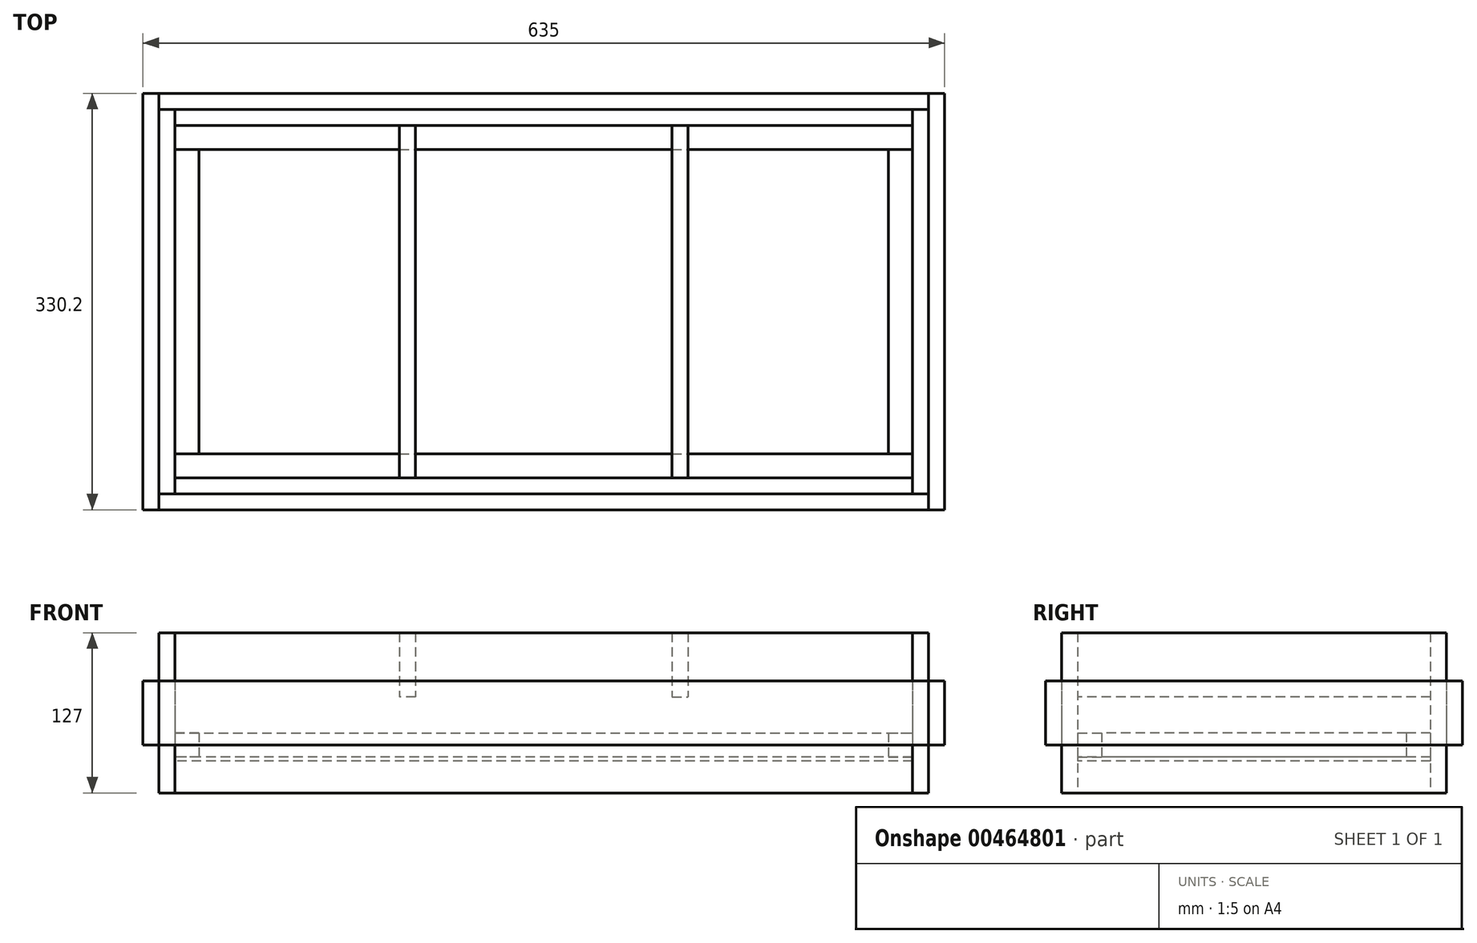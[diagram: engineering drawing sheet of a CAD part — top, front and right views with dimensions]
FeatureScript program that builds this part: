
annotation { "Feature Type Name" : "Feature", "Feature Type Description" : "" }
export const myFeature = defineFeature(function(context is Context, id is Id, definition is map)
    precondition{}
    {
        {
            var Q0;
            Q0=qCreatedBy(makeId("Top.planeOp"),FACE);
            var sketch = newSketch(context, id + "F0", { "sketchPlane" : qUnion([Q0])});
            skLineSegment(sketch, "E0.bottom", {"start": v(292.1, 139.7) * mm, "end": v(-292.1, 139.7) * mm});
            skLineSegment(sketch, "E0.top", {"start": v(292.1, -139.7) * mm, "end": v(-292.1, -139.7) * mm});
            skLineSegment(sketch, "E0.left", {"start": v(292.1, 139.7) * mm, "end": v(292.1, -139.7) * mm});
            skLineSegment(sketch, "E0.right", {"start": v(-292.1, 139.7) * mm, "end": v(-292.1, -139.7) * mm});
            skPoint(sketch, "E0.middle", {"position": v(0, 0) * mm});
            skLineSegment(sketch, "E1", {"start": v(-292.1, 0) * mm, "end": v(292.1, 0) * mm, "construction": true});
            skLineSegment(sketch, "E2", {"start": v(0, 139.7) * mm, "end": v(0, -139.7) * mm, "construction": true});
            skSolve(sketch);
        }
        {
            var Q0;
            Q0 = qSketchRegion(id + "F0", true);
            extrude(context, id + "F1", {"entities" : qUnion([Q0]), "depth" : 3.17 * mm});
        }
        {
            var Q0;
            Q0=qCreatedBy(makeId("Top.planeOp"),FACE);
            var sketch = newSketch(context, id + "F2", { "sketchPlane" : qUnion([Q0])});
            skLineSegment(sketch, "E3.bottom", {"start": v(-292.1, 139.7) * mm, "end": v(292.1, 139.7) * mm});
            skLineSegment(sketch, "E3.top", {"start": v(-292.1, 152.4) * mm, "end": v(292.1, 152.4) * mm});
            skLineSegment(sketch, "E3.left", {"start": v(-292.1, 139.7) * mm, "end": v(-292.1, 152.4) * mm});
            skLineSegment(sketch, "E3.right", {"start": v(292.1, 139.7) * mm, "end": v(292.1, 152.4) * mm});
            skSolve(sketch);
        }
        {
            var Q0;
            Q0 = qSketchRegion(id + "F2", true);
            extrude(context, id + "F3", {"entities" : qUnion([Q0]), "depth" : 101.6 * mm, "hasSecondDirection" : true, "secondDirectionOppositeDirection" : true, "secondDirectionDepth" : 25.4 * mm});
        }
        {
            var Q0;
            Q0=makeQuery(id+"F3.opExtrude","SWEPT_BODY",BODY,{"disambiguationData":[OSD([sQuery(id+"F2.wireOp",EDGE,"E3.bottom"),sQuery(id+"F2.wireOp",EDGE,"E3.top"),sQuery(id+"F2.wireOp",EDGE,"E3.left"),sQuery(id+"F2.wireOp",EDGE,"E3.right")])]});
            var Q1;
            Q1=qCreatedBy(makeId("Front.planeOp"),FACE);
            mirror(context, id + "F4", {"entities" : qUnion([Q0]), "mirrorPlane" : qUnion([Q1])});
        }
        {
            var Q0;
            Q0=qCreatedBy(makeId("Top.planeOp"),FACE);
            var sketch = newSketch(context, id + "F5", { "sketchPlane" : qUnion([Q0])});
            skLineSegment(sketch, "E4.bottom", {"start": v(292.1, 152.4) * mm, "end": v(304.8, 152.4) * mm});
            skLineSegment(sketch, "E4.top", {"start": v(292.1, -152.4) * mm, "end": v(304.8, -152.4) * mm});
            skLineSegment(sketch, "E4.left", {"start": v(292.1, 152.4) * mm, "end": v(292.1, -152.4) * mm});
            skLineSegment(sketch, "E4.right", {"start": v(304.8, 152.4) * mm, "end": v(304.8, -152.4) * mm});
            skSolve(sketch);
        }
        {
            var Q0;
            Q0 = qSketchRegion(id + "F5", true);
            extrude(context, id + "F6", {"entities" : qUnion([Q0]), "depth" : 101.6 * mm, "hasSecondDirection" : true, "secondDirectionOppositeDirection" : true, "secondDirectionDepth" : 25.4 * mm});
        }
        {
            var Q0;
            Q0=makeQuery(id+"F6.opExtrude","SWEPT_BODY",BODY,{"disambiguationData":[OSD([sQuery(id+"F5.wireOp",EDGE,"E4.bottom"),sQuery(id+"F5.wireOp",EDGE,"E4.top"),sQuery(id+"F5.wireOp",EDGE,"E4.left"),sQuery(id+"F5.wireOp",EDGE,"E4.right")])]});
            var Q1;
            Q1=qCreatedBy(makeId("Right.planeOp"),FACE);
            mirror(context, id + "F7", {"entities" : qUnion([Q0]), "mirrorPlane" : qUnion([Q1])});
        }
        {
            var Q0;
            Q0=qCreatedBy(makeId("Top.planeOp"),FACE);
            var sketch = newSketch(context, id + "F8", { "sketchPlane" : qUnion([Q0])});
            skLineSegment(sketch, "E5.bottom", {"start": v(-304.8, 165.1) * mm, "end": v(304.8, 165.1) * mm});
            skLineSegment(sketch, "E5.top", {"start": v(-304.8, 152.4) * mm, "end": v(304.8, 152.4) * mm});
            skLineSegment(sketch, "E5.left", {"start": v(-304.8, 165.1) * mm, "end": v(-304.8, 152.4) * mm});
            skLineSegment(sketch, "E5.right", {"start": v(304.8, 165.1) * mm, "end": v(304.8, 152.4) * mm});
            skSolve(sketch);
        }
        {
            var Q0;
            Q0 = qSketchRegion(id + "F8", true);
            extrude(context, id + "F9", {"entities" : qUnion([Q0]), "depth" : 63.5 * mm, "hasSecondDirection" : true, "secondDirectionOppositeDirection" : false, "secondDirectionDepth" : 12.7 * mm});
        }
        {
            var Q0;
            Q0=makeQuery(id+"F9.opExtrude","SWEPT_BODY",BODY,{"disambiguationData":[OSD([sQuery(id+"F8.wireOp",EDGE,"E5.bottom"),sQuery(id+"F8.wireOp",EDGE,"E5.top"),sQuery(id+"F8.wireOp",EDGE,"E5.left"),sQuery(id+"F8.wireOp",EDGE,"E5.right")])]});
            var Q1;
            Q1=qCreatedBy(makeId("Front.planeOp"),FACE);
            mirror(context, id + "F10", {"entities" : qUnion([Q0]), "mirrorPlane" : qUnion([Q1])});
        }
        {
            var Q0;
            Q0=qCreatedBy(makeId("Top.planeOp"),FACE);
            var sketch = newSketch(context, id + "F11", { "sketchPlane" : qUnion([Q0])});
            skLineSegment(sketch, "E6.bottom", {"start": v(304.8, 165.1) * mm, "end": v(317.5, 165.1) * mm});
            skLineSegment(sketch, "E6.top", {"start": v(304.8, -165.1) * mm, "end": v(317.5, -165.1) * mm});
            skLineSegment(sketch, "E6.left", {"start": v(304.8, 165.1) * mm, "end": v(304.8, -165.1) * mm});
            skLineSegment(sketch, "E6.right", {"start": v(317.5, 165.1) * mm, "end": v(317.5, -165.1) * mm});
            skSolve(sketch);
        }
        {
            var Q0;
            Q0 = qSketchRegion(id + "F11", true);
            extrude(context, id + "F12", {"entities" : qUnion([Q0]), "depth" : 63.5 * mm, "hasSecondDirection" : true, "secondDirectionOppositeDirection" : false, "secondDirectionDepth" : 12.7 * mm});
        }
        {
            var Q0;
            Q0=makeQuery(id+"F12.opExtrude","SWEPT_BODY",BODY,{"disambiguationData":[OSD([sQuery(id+"F11.wireOp",EDGE,"E6.bottom"),sQuery(id+"F11.wireOp",EDGE,"E6.top"),sQuery(id+"F11.wireOp",EDGE,"E6.left"),sQuery(id+"F11.wireOp",EDGE,"E6.right")])]});
            var Q1;
            Q1=qCreatedBy(makeId("Right.planeOp"),FACE);
            mirror(context, id + "F13", {"entities" : qUnion([Q0]), "mirrorPlane" : qUnion([Q1])});
        }
        {
            var Q0;
            Q0=qCreatedBy(makeId("Top.planeOp"),FACE);
            var sketch = newSketch(context, id + "F14", { "sketchPlane" : qUnion([Q0])});
            skLineSegment(sketch, "E7.bottom", {"start": v(101.6, 139.7) * mm, "end": v(114.3, 139.7) * mm});
            skLineSegment(sketch, "E7.top", {"start": v(101.6, -139.7) * mm, "end": v(114.3, -139.7) * mm});
            skLineSegment(sketch, "E7.left", {"start": v(101.6, 139.7) * mm, "end": v(101.6, -139.7) * mm});
            skLineSegment(sketch, "E7.right", {"start": v(114.3, 139.7) * mm, "end": v(114.3, -139.7) * mm});
            skSolve(sketch);
        }
        {
            var Q0;
            Q0 = qSketchRegion(id + "F14", true);
            extrude(context, id + "F15", {"entities" : qUnion([Q0]), "depth" : 101.6 * mm, "hasSecondDirection" : true, "secondDirectionOppositeDirection" : false, "secondDirectionDepth" : 50.8 * mm});
        }
        {
            var Q0;
            Q0=makeQuery(id+"F15.opExtrude","SWEPT_BODY",BODY,{"disambiguationData":[OSD([sQuery(id+"F14.wireOp",EDGE,"E7.bottom"),sQuery(id+"F14.wireOp",EDGE,"E7.top"),sQuery(id+"F14.wireOp",EDGE,"E7.left"),sQuery(id+"F14.wireOp",EDGE,"E7.right")])]});
            var Q1;
            Q1=qCreatedBy(makeId("Right.planeOp"),FACE);
            mirror(context, id + "F16", {"entities" : qUnion([Q0]), "mirrorPlane" : qUnion([Q1])});
        }
        {
            var Q0;
            Q0=qCreatedBy(makeId("Top.planeOp"),FACE);
            var sketch = newSketch(context, id + "F17", { "sketchPlane" : qUnion([Q0])});
            skLineSegment(sketch, "E8.bottom", {"start": v(-292.1, 139.7) * mm, "end": v(292.1, 139.7) * mm});
            skLineSegment(sketch, "E8.top", {"start": v(-292.1, 120.65) * mm, "end": v(292.1, 120.65) * mm});
            skLineSegment(sketch, "E8.left", {"start": v(-292.1, 139.7) * mm, "end": v(-292.1, 120.65) * mm});
            skLineSegment(sketch, "E8.right", {"start": v(292.1, 139.7) * mm, "end": v(292.1, 120.65) * mm});
            skSolve(sketch);
        }
        {
            var Q0;
            Q0 = qSketchRegion(id + "F17", true);
            extrude(context, id + "F18", {"entities" : qUnion([Q0]), "depth" : 22.22 * mm, "hasSecondDirection" : true, "secondDirectionOppositeDirection" : false, "secondDirectionDepth" : 3.17 * mm});
        }
        {
            var Q0;
            Q0=makeQuery(id+"F18.opExtrude","SWEPT_BODY",BODY,{"disambiguationData":[OSD([sQuery(id+"F17.wireOp",EDGE,"E8.bottom"),sQuery(id+"F17.wireOp",EDGE,"E8.top"),sQuery(id+"F17.wireOp",EDGE,"E8.left"),sQuery(id+"F17.wireOp",EDGE,"E8.right")])]});
            var Q1;
            Q1=qCreatedBy(makeId("Front.planeOp"),FACE);
            mirror(context, id + "F19", {"entities" : qUnion([Q0]), "mirrorPlane" : qUnion([Q1])});
        }
        {
            var Q0;
            Q0=qCreatedBy(makeId("Top.planeOp"),FACE);
            var sketch = newSketch(context, id + "F20", { "sketchPlane" : qUnion([Q0])});
            skLineSegment(sketch, "E9.bottom", {"start": v(273.05, 120.65) * mm, "end": v(292.1, 120.65) * mm});
            skLineSegment(sketch, "E9.top", {"start": v(273.05, -120.65) * mm, "end": v(292.1, -120.65) * mm});
            skLineSegment(sketch, "E9.left", {"start": v(273.05, 120.65) * mm, "end": v(273.05, -120.65) * mm});
            skLineSegment(sketch, "E9.right", {"start": v(292.1, 120.65) * mm, "end": v(292.1, -120.65) * mm});
            skSolve(sketch);
        }
        {
            var Q0;
            Q0 = qSketchRegion(id + "F20", true);
            extrude(context, id + "F21", {"entities" : qUnion([Q0]), "depth" : 22.22 * mm, "hasSecondDirection" : true, "secondDirectionOppositeDirection" : false, "secondDirectionDepth" : 3.17 * mm});
        }
        {
            var Q0;
            Q0=makeQuery(id+"F21.opExtrude","SWEPT_BODY",BODY,{"disambiguationData":[OSD([sQuery(id+"F20.wireOp",EDGE,"E9.bottom"),sQuery(id+"F20.wireOp",EDGE,"E9.top"),sQuery(id+"F20.wireOp",EDGE,"E9.left"),sQuery(id+"F20.wireOp",EDGE,"E9.right")])]});
            var Q1;
            Q1=qCreatedBy(makeId("Right.planeOp"),FACE);
            mirror(context, id + "F22", {"entities" : qUnion([Q0]), "mirrorPlane" : qUnion([Q1])});
        }
    });
